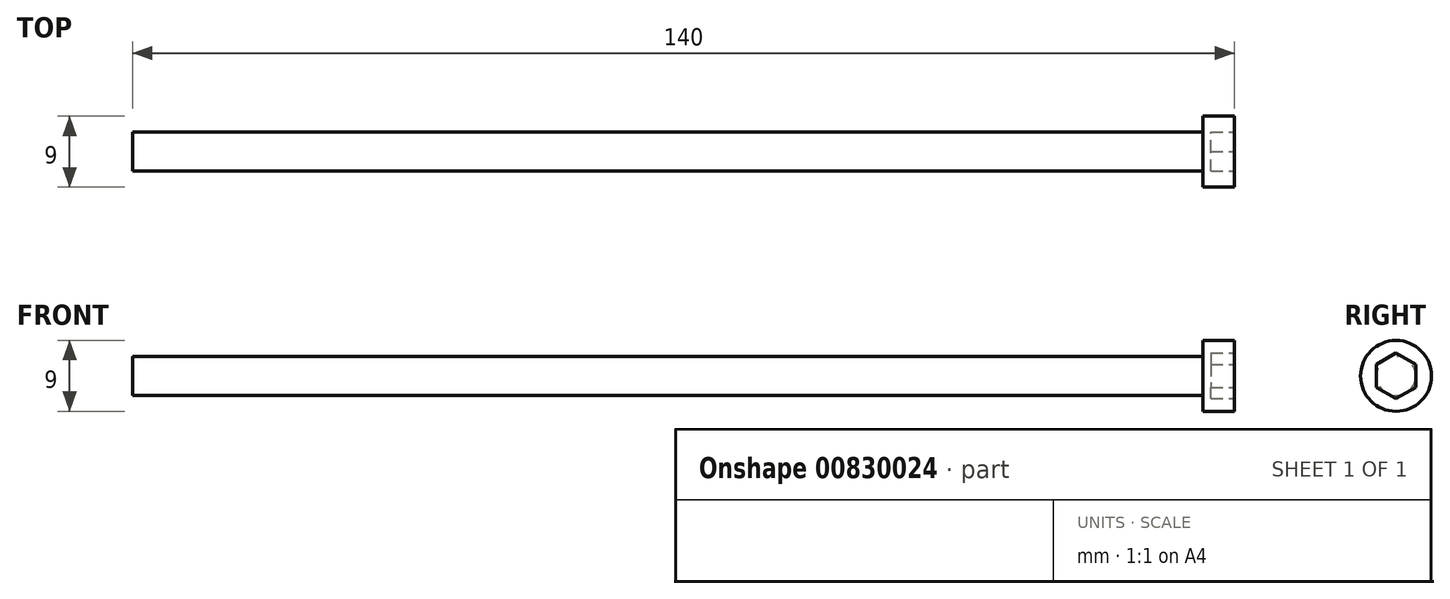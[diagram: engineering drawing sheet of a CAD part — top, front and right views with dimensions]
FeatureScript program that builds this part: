
annotation { "Feature Type Name" : "Feature", "Feature Type Description" : "" }
export const myFeature = defineFeature(function(context is Context, id is Id, definition is map)
    precondition{}
    {
        {
            var Q0;
            Q0=qCreatedBy(makeId("Top.planeOp"),FACE);
            var sketch = newSketch(context, id + "F0", { "sketchPlane" : qUnion([Q0])});
            skLineSegment(sketch, "E0", {"start": v(-140, 2.5) * mm, "end": v(-4, 2.5) * mm});
            skLineSegment(sketch, "E1", {"start": v(-4, 2.5) * mm, "end": v(-4, 4.5) * mm});
            skLineSegment(sketch, "E2", {"start": v(-4, 4.5) * mm, "end": v(0, 4.5) * mm});
            skLineSegment(sketch, "E3", {"start": v(0, 4.5) * mm, "end": v(0, 0) * mm});
            skLineSegment(sketch, "E4", {"start": v(0, 0) * mm, "end": v(-140, 0) * mm});
            skLineSegment(sketch, "E5", {"start": v(-140, 0) * mm, "end": v(-140, 2.5) * mm});
            skSolve(sketch);
        }
        {
            var Q0;
            Q0=makeQuery(id+"F0.imprint","IMPRINT",FACE,{"disambiguationData":[TD([[makeQuery(id+"F0.imprint","IMPRINT",EDGE,{"derivedFrom":sQuery(id+"F0.wireOp",EDGE,"E0")}),-1.0]])]});
            var Q1;
            Q1=sQuery(id+"F0.wireOp",EDGE,"E4");
            revolve(context, id + "F1", {"surfaceOperationType" : NewSurfaceOperationType.NEW, "entities" : qUnion([Q0]), "axis" : qUnion([Q1]), "revolveType" : RevolveType.FULL});
        }
        {
            var Q0;
            Q0=makeQuery(id+"F1.opRevolve","SWEPT_FACE",FACE,{"disambiguationData":[OSD([sQuery(id+"F0.wireOp",EDGE,"E3")])]});
            var sketch = newSketch(context, id + "F2", { "sketchPlane" : qUnion([Q0])});
            skCircle(sketch, "E6.cCircle", {"center": v(0, 0) * mm, "radius": 2.5 * mm, "construction": true});
            skLineSegment(sketch, "E6.0", {"start": v(2.5, 1.44) * mm, "end": v(2.5, -1.44) * mm});
            skLineSegment(sketch, "E6.1", {"start": v(2.5, -1.44) * mm, "end": v(0, -2.89) * mm});
            skLineSegment(sketch, "E6.2", {"start": v(0, -2.89) * mm, "end": v(-2.5, -1.44) * mm});
            skLineSegment(sketch, "E6.3", {"start": v(-2.5, -1.44) * mm, "end": v(-2.5, 1.44) * mm});
            skLineSegment(sketch, "E6.4", {"start": v(-2.5, 1.44) * mm, "end": v(0, 2.89) * mm});
            skLineSegment(sketch, "E6.5", {"start": v(0, 2.89) * mm, "end": v(2.5, 1.44) * mm});
            skPoint(sketch, "E6.0.midPoint", {"position": v(2.5, 0) * mm});
            skSolve(sketch);
        }
        {
            var Q0;
            Q0=makeQuery(id+"F2.imprint","IMPRINT",FACE,{"disambiguationData":[TD([[makeQuery(id+"F2.imprint","IMPRINT",EDGE,{"derivedFrom":sQuery(id+"F2.wireOp",EDGE,"E6.0")}),-1.0]])]});
            extrude(context, id + "F3", {"entities" : qUnion([Q0]), "operationType" : NewBodyOperationType.REMOVE, "oppositeDirection" : true, "depth" : 3 * mm, "offsetDistance" : 25 * mm});
        }
    });
